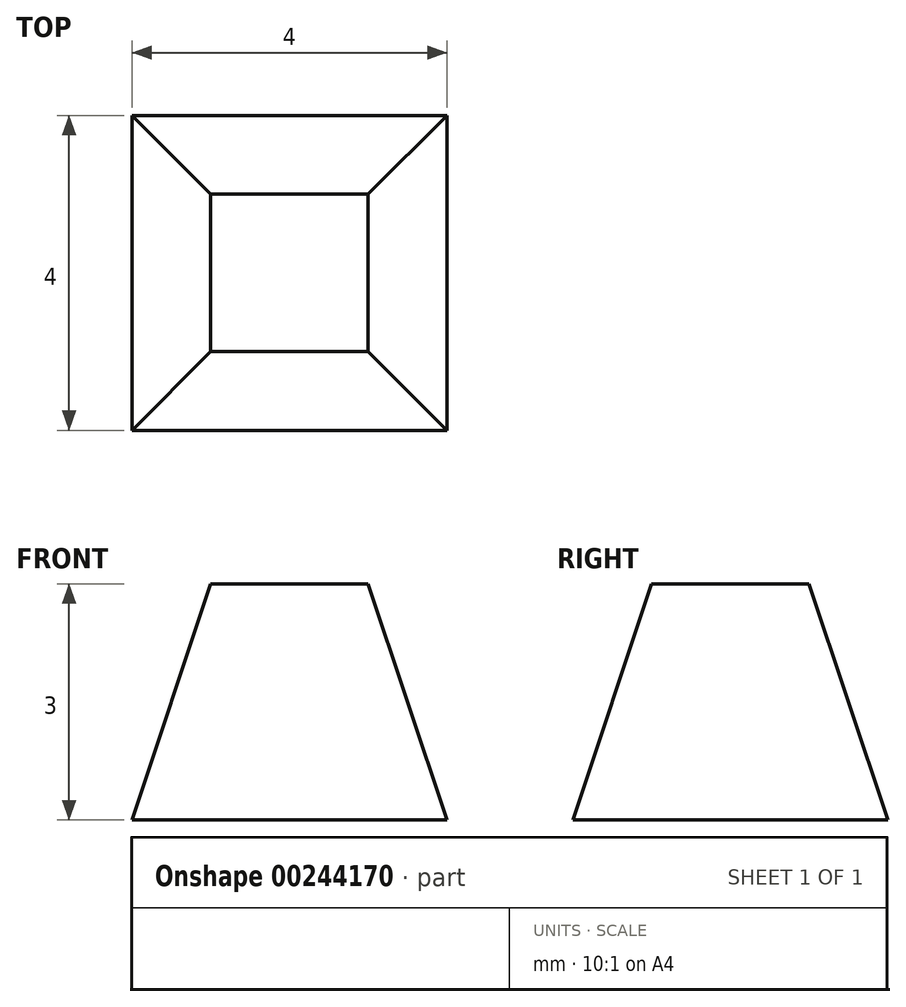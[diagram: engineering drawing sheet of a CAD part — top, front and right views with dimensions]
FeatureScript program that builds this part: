
annotation { "Feature Type Name" : "Feature", "Feature Type Description" : "" }
export const myFeature = defineFeature(function(context is Context, id is Id, definition is map)
    precondition{}
    {
        {
            var Q0;
            Q0=qCreatedBy(makeId("Top.planeOp"),FACE);
            var sketch = newSketch(context, id + "F0", { "sketchPlane" : qUnion([Q0])});
            skLineSegment(sketch, "E0.bottom", {"start": v(0, 0) * mm, "end": v(4, 0) * mm});
            skLineSegment(sketch, "E0.top", {"start": v(0, 4) * mm, "end": v(4, 4) * mm});
            skLineSegment(sketch, "E0.left", {"start": v(0, 0) * mm, "end": v(0, 4) * mm});
            skLineSegment(sketch, "E0.right", {"start": v(4, 0) * mm, "end": v(4, 4) * mm});
            skSolve(sketch);
        }
        {
            var Q0;
            Q0 = qSketchRegion(id + "F0", true);
            extrude(context, id + "F1", {"entities" : qUnion([Q0]), "depth" : 3 * mm});
        }
        {
            var Q0;
            Q0=makeQuery(id+"F1.opExtrude","SWEPT_FACE",FACE,{"disambiguationData":[OSD([sQuery(id+"F0.wireOp",EDGE,"E0.bottom")])]});
            var sketch = newSketch(context, id + "F2", { "sketchPlane" : qUnion([Q0])});
            skLineSegment(sketch, "E1", {"start": v(4, 0) * mm, "end": v(4, 3) * mm});
            skLineSegment(sketch, "E2", {"start": v(4, 3) * mm, "end": v(3, 3) * mm});
            skLineSegment(sketch, "E3", {"start": v(3, 3) * mm, "end": v(4, 0) * mm});
            skLineSegment(sketch, "E4", {"start": v(0, 0) * mm, "end": v(0, 3) * mm});
            skLineSegment(sketch, "E5", {"start": v(0, 3) * mm, "end": v(1, 3) * mm});
            skLineSegment(sketch, "E6", {"start": v(1, 3) * mm, "end": v(0, 0) * mm});
            skSolve(sketch);
        }
        {
            var Q0;
            Q0 = qSketchRegion(id + "F2", true);
            extrude(context, id + "F3", {"entities" : qUnion([Q0]), "operationType" : NewBodyOperationType.REMOVE, "oppositeDirection" : true, "depth" : 25 * mm});
        }
        {
            var Q0;
            Q0=qCreatedBy(makeId("Right.planeOp"),FACE);
            var sketch = newSketch(context, id + "F4", { "sketchPlane" : qUnion([Q0])});
            skLineSegment(sketch, "E7", {"start": v(0, 0) * mm, "end": v(0, 3) * mm});
            skLineSegment(sketch, "E8", {"start": v(0, 3) * mm, "end": v(1, 3) * mm});
            skLineSegment(sketch, "E9", {"start": v(1, 3) * mm, "end": v(0, 0) * mm});
            skLineSegment(sketch, "E10", {"start": v(0, 0) * mm, "end": v(4, 0) * mm});
            skLineSegment(sketch, "E11", {"start": v(4, 0) * mm, "end": v(4, 3) * mm});
            skLineSegment(sketch, "E12", {"start": v(4, 3) * mm, "end": v(3, 3) * mm});
            skLineSegment(sketch, "E13", {"start": v(3, 3) * mm, "end": v(4, 0) * mm});
            skSolve(sketch);
        }
        {
            var Q0;
            Q0 = qSketchRegion(id + "F4", true);
            extrude(context, id + "F5", {"entities" : qUnion([Q0]), "operationType" : NewBodyOperationType.REMOVE, "depth" : 25 * mm});
        }
    });
